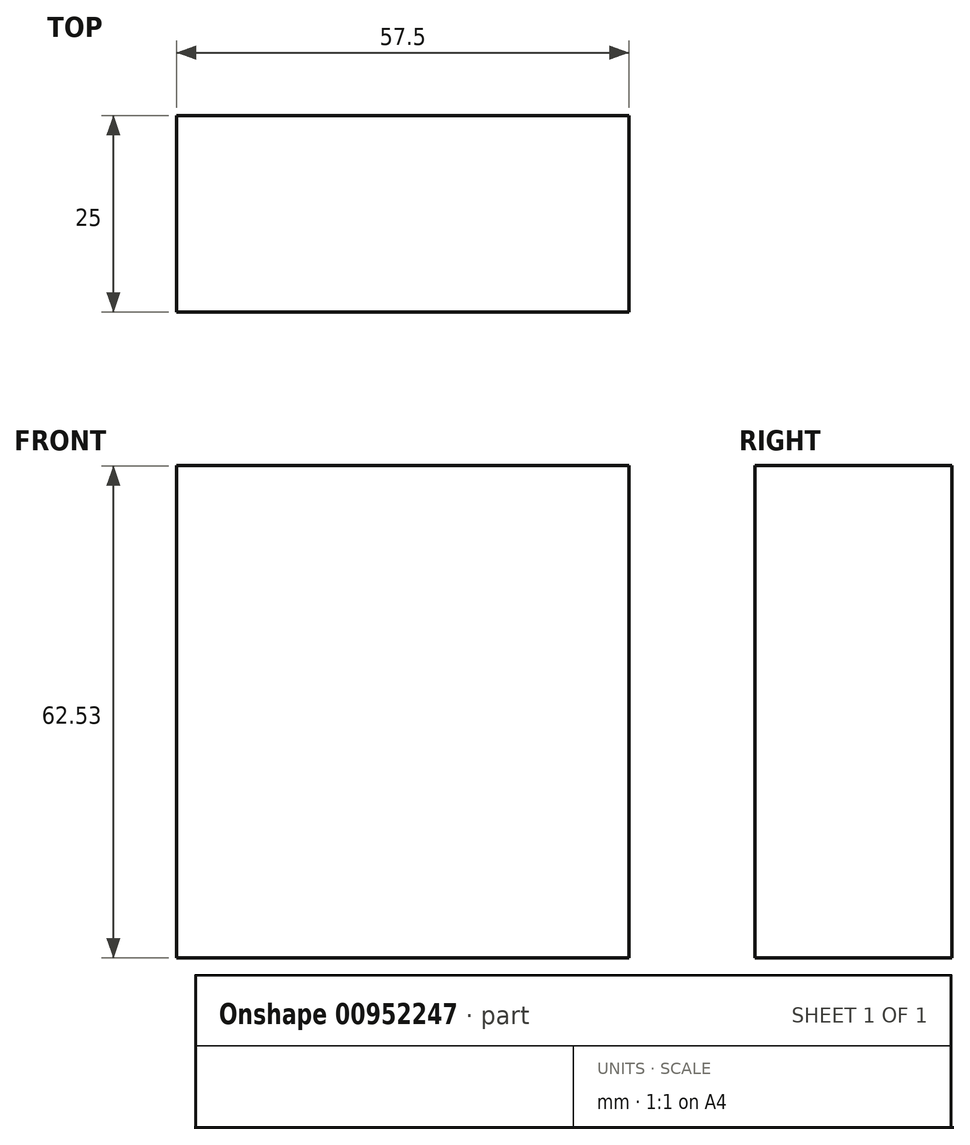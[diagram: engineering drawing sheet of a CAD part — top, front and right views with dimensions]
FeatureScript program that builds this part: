
annotation { "Feature Type Name" : "Feature", "Feature Type Description" : "" }
export const myFeature = defineFeature(function(context is Context, id is Id, definition is map)
    precondition{}
    {
        {
            var Q0;
            Q0=qCreatedBy(makeId("Front.planeOp"),FACE);
            var sketch = newSketch(context, id + "F0", { "sketchPlane" : qUnion([Q0])});
            skLineSegment(sketch, "E0.bottom", {"start": v(-28.07, 45.78) * mm, "end": v(29.43, 45.78) * mm});
            skLineSegment(sketch, "E0.top", {"start": v(-28.07, -16.75) * mm, "end": v(29.43, -16.75) * mm});
            skLineSegment(sketch, "E0.left", {"start": v(-28.07, 45.78) * mm, "end": v(-28.07, -16.75) * mm});
            skLineSegment(sketch, "E0.right", {"start": v(29.43, 45.78) * mm, "end": v(29.43, -16.75) * mm});
            skSolve(sketch);
        }
        {
            var Q0;
            Q0 = qSketchRegion(id + "F0", true);
            extrude(context, id + "F1", {"entities" : qUnion([Q0]), "depth" : 25 * mm, "offsetDistance" : 25 * mm});
        }
    });
